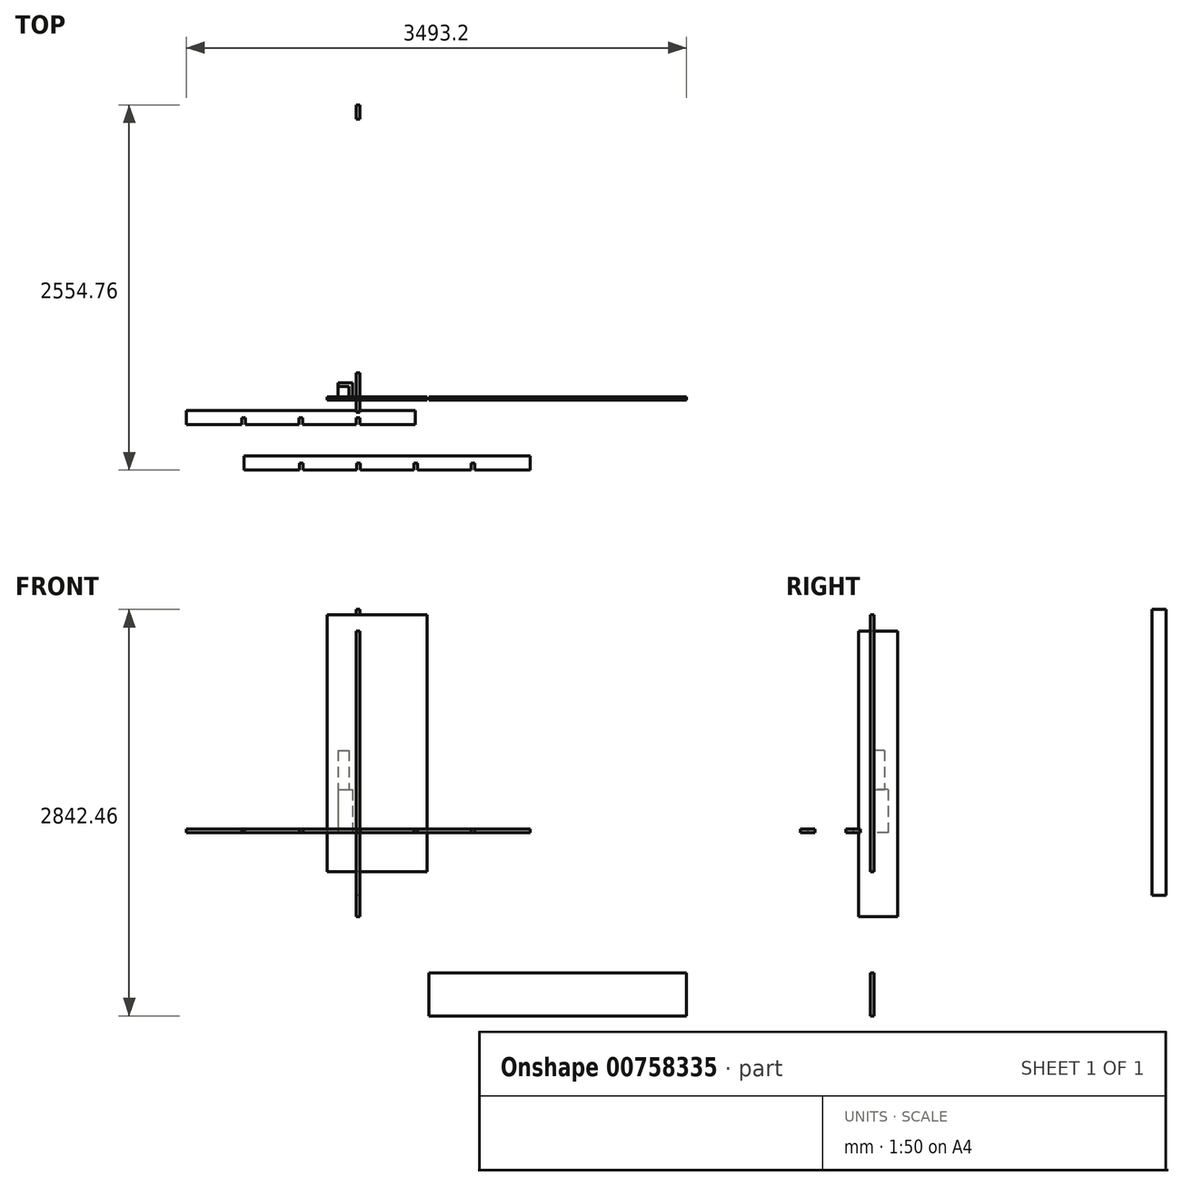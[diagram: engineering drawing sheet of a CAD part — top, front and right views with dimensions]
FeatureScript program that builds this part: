
annotation { "Feature Type Name" : "Feature", "Feature Type Description" : "" }
export const myFeature = defineFeature(function(context is Context, id is Id, definition is map)
    precondition{}
    {
        {
            var Q0;
            Q0=qCreatedBy(makeId("Top.planeOp"),FACE);
            var sketch = newSketch(context, id + "F0", { "sketchPlane" : qUnion([Q0])});
            skLineSegment(sketch, "E0.bottom", {"start": v(-127.05, 96.6) * mm, "end": v(-27.05, 96.6) * mm});
            skLineSegment(sketch, "E0.top", {"start": v(-127.05, -3.4) * mm, "end": v(-27.05, -3.4) * mm});
            skLineSegment(sketch, "E0.left", {"start": v(-127.05, 96.6) * mm, "end": v(-127.05, -3.4) * mm});
            skLineSegment(sketch, "E0.right", {"start": v(-27.05, 96.6) * mm, "end": v(-27.05, -3.4) * mm});
            skSolve(sketch);
        }
        {
            var Q0;
            Q0 = qSketchRegion(id + "F0", true);
            extrude(context, id + "F1", {"entities" : qUnion([Q0]), "depth" : 300 * mm, "offsetDistance" : 25 * mm});
        }
        {
            var Q0;
            Q0=makeQuery(id+"F1.opExtrude","CAP_FACE",FACE,{"disambiguationData":[OSD([sQuery(id+"F0.wireOp",EDGE,"E0.bottom"),sQuery(id+"F0.wireOp",EDGE,"E0.top"),sQuery(id+"F0.wireOp",EDGE,"E0.left"),sQuery(id+"F0.wireOp",EDGE,"E0.right")])],"isStart":false});
            var sketch = newSketch(context, id + "F2", { "sketchPlane" : qUnion([Q0])});
            skLineSegment(sketch, "E1.bottom", {"start": v(-127.05, -3.4) * mm, "end": v(-52.05, -3.4) * mm});
            skLineSegment(sketch, "E1.top", {"start": v(-127.05, 71.6) * mm, "end": v(-52.05, 71.6) * mm});
            skLineSegment(sketch, "E1.left", {"start": v(-127.05, -3.4) * mm, "end": v(-127.05, 71.6) * mm});
            skLineSegment(sketch, "E1.right", {"start": v(-52.05, -3.4) * mm, "end": v(-52.05, 71.6) * mm});
            skSolve(sketch);
        }
        {
            var Q0;
            Q0=makeQuery(id+"F2.imprint","IMPRINT",FACE,{"disambiguationData":[TD([[makeQuery(id+"F2.imprint","IMPRINT",EDGE,{"derivedFrom":sQuery(id+"F2.wireOp",EDGE,"E1.bottom")}),1.0]])]});
            extrude(context, id + "F3", {"entities" : qUnion([Q0]), "operationType" : NewBodyOperationType.ADD, "depth" : 275 * mm, "offsetDistance" : 25 * mm});
        }
        {
            var Q0;
            Q0=qCreatedBy(makeId("Front.planeOp"),FACE);
            var sketch = newSketch(context, id + "F4", { "sketchPlane" : qUnion([Q0])});
            skLineSegment(sketch, "E2.bottom", {"start": v(495.05, 1524.66) * mm, "end": v(-204.95, 1524.66) * mm});
            skLineSegment(sketch, "E2.top", {"start": v(495.05, -275.34) * mm, "end": v(-204.95, -275.34) * mm});
            skLineSegment(sketch, "E2.left", {"start": v(495.05, 1524.66) * mm, "end": v(495.05, -275.34) * mm});
            skLineSegment(sketch, "E2.right", {"start": v(-204.95, 1524.66) * mm, "end": v(-204.95, -275.34) * mm});
            skSolve(sketch);
        }
        {
            var Q0;
            Q0=makeQuery(id+"F4.imprint","IMPRINT",FACE,{"disambiguationData":[TD([[makeQuery(id+"F4.imprint","IMPRINT",EDGE,{"derivedFrom":sQuery(id+"F4.wireOp",EDGE,"E2.bottom")}),1.0]])]});
            extrude(context, id + "F5", {"entities" : qUnion([Q0]), "depth" : 25 * mm, "offsetDistance" : 25 * mm});
        }
        {
            var Q0;
            Q0=qCreatedBy(makeId("Right.planeOp"),FACE);
            var sketch = newSketch(context, id + "F6", { "sketchPlane" : qUnion([Q0])});
            skLineSegment(sketch, "E3.bottom", {"start": v(165.35, 1410.5) * mm, "end": v(-109.65, 1410.5) * mm});
            skLineSegment(sketch, "E3.top", {"start": v(165.35, -589.5) * mm, "end": v(-109.65, -589.5) * mm});
            skLineSegment(sketch, "E3.left", {"start": v(165.35, 1410.5) * mm, "end": v(165.35, -589.5) * mm});
            skLineSegment(sketch, "E3.right", {"start": v(-109.65, 1410.5) * mm, "end": v(-109.65, -589.5) * mm});
            skSolve(sketch);
        }
        {
            var Q0;
            Q0=makeQuery(id+"F6.imprint","IMPRINT",FACE,{"disambiguationData":[TD([[makeQuery(id+"F6.imprint","IMPRINT",EDGE,{"derivedFrom":sQuery(id+"F6.wireOp",EDGE,"E3.bottom")}),1.0]])]});
            extrude(context, id + "F7", {"entities" : qUnion([Q0]), "depth" : 25 * mm, "offsetDistance" : 25 * mm});
        }
        {
            var Q0;
            Q0=qCreatedBy(makeId("Front.planeOp"),FACE);
            var sketch = newSketch(context, id + "F8", { "sketchPlane" : qUnion([Q0])});
            skLineSegment(sketch, "E4.bottom", {"start": v(2305.7, -982.24) * mm, "end": v(505.7, -982.24) * mm});
            skLineSegment(sketch, "E4.top", {"start": v(2305.7, -1282.24) * mm, "end": v(505.7, -1282.24) * mm});
            skLineSegment(sketch, "E4.left", {"start": v(2305.7, -982.24) * mm, "end": v(2305.7, -1282.24) * mm});
            skLineSegment(sketch, "E4.right", {"start": v(505.7, -982.24) * mm, "end": v(505.7, -1282.24) * mm});
            skSolve(sketch);
        }
        {
            var Q0;
            Q0=makeQuery(id+"F8.imprint","IMPRINT",FACE,{"disambiguationData":[TD([[makeQuery(id+"F8.imprint","IMPRINT",EDGE,{"derivedFrom":sQuery(id+"F8.wireOp",EDGE,"E4.bottom")}),1.0]])]});
            extrude(context, id + "F9", {"entities" : qUnion([Q0]), "depth" : 25 * mm, "offsetDistance" : 25 * mm});
        }
        {
            var Q0;
            Q0=qCreatedBy(makeId("Right.planeOp"),FACE);
            var sketch = newSketch(context, id + "F10", { "sketchPlane" : qUnion([Q0])});
            skLineSegment(sketch, "E5.bottom", {"start": v(2041.36, 1560.22) * mm, "end": v(1941.36, 1560.22) * mm});
            skLineSegment(sketch, "E5.top", {"start": v(2041.36, -439.78) * mm, "end": v(1941.36, -439.78) * mm});
            skLineSegment(sketch, "E5.left", {"start": v(2041.36, 1560.22) * mm, "end": v(2041.36, -439.78) * mm});
            skLineSegment(sketch, "E5.right", {"start": v(1941.36, 1560.22) * mm, "end": v(1941.36, -439.78) * mm});
            skSolve(sketch);
        }
        {
            var Q0;
            Q0=makeQuery(id+"F10.imprint","IMPRINT",FACE,{"disambiguationData":[TD([[makeQuery(id+"F10.imprint","IMPRINT",EDGE,{"derivedFrom":sQuery(id+"F10.wireOp",EDGE,"E5.bottom")}),1.0]])]});
            extrude(context, id + "F11", {"entities" : qUnion([Q0]), "depth" : 25 * mm, "offsetDistance" : 25 * mm});
        }
        {
            var Q0;
            Q0=qCreatedBy(makeId("Top.planeOp"),FACE);
            var sketch = newSketch(context, id + "F12", { "sketchPlane" : qUnion([Q0])});
            skLineSegment(sketch, "E6", {"start": v(412.5, -196.5) * mm, "end": v(25, -196.5) * mm});
            skLineSegment(sketch, "E7", {"start": v(25, -196.5) * mm, "end": v(25, -146.5) * mm});
            skLineSegment(sketch, "E8", {"start": v(25, -146.5) * mm, "end": v(0, -146.5) * mm});
            skLineSegment(sketch, "E9", {"start": v(0, -146.5) * mm, "end": v(0, -196.5) * mm});
            skLineSegment(sketch, "E10", {"start": v(0, -196.5) * mm, "end": v(-375, -196.5) * mm});
            skLineSegment(sketch, "E11", {"start": v(-375, -196.5) * mm, "end": v(-375, -146.5) * mm});
            skLineSegment(sketch, "E12", {"start": v(-375, -146.5) * mm, "end": v(-400, -146.5) * mm});
            skLineSegment(sketch, "E13", {"start": v(-400, -146.5) * mm, "end": v(-400, -196.5) * mm});
            skLineSegment(sketch, "E14", {"start": v(-400, -196.5) * mm, "end": v(-775, -196.5) * mm});
            skLineSegment(sketch, "E15", {"start": v(-775, -196.5) * mm, "end": v(-775, -146.5) * mm});
            skLineSegment(sketch, "E16", {"start": v(-775, -146.5) * mm, "end": v(-800, -146.5) * mm});
            skLineSegment(sketch, "E17", {"start": v(-800, -146.5) * mm, "end": v(-800, -196.5) * mm});
            skLineSegment(sketch, "E18", {"start": v(-800, -196.5) * mm, "end": v(-1187.5, -196.5) * mm});
            skLineSegment(sketch, "E19", {"start": v(-1187.5, -196.5) * mm, "end": v(-1187.5, -96.5) * mm});
            skLineSegment(sketch, "E20", {"start": v(-1187.5, -96.5) * mm, "end": v(412.5, -96.5) * mm});
            skLineSegment(sketch, "E21", {"start": v(412.5, -96.5) * mm, "end": v(412.5, -196.5) * mm});
            skSolve(sketch);
        }
        {
            var Q0;
            Q0=makeQuery(id+"F12.imprint","IMPRINT",FACE,{"disambiguationData":[TD([[makeQuery(id+"F12.imprint","IMPRINT",EDGE,{"derivedFrom":sQuery(id+"F12.wireOp",EDGE,"E6")}),-1.0]])]});
            extrude(context, id + "F13", {"entities" : qUnion([Q0]), "depth" : 25 * mm, "offsetDistance" : 25 * mm});
        }
        {
            var Q0;
            Q0=qCreatedBy(makeId("Top.planeOp"),FACE);
            var sketch = newSketch(context, id + "F14", { "sketchPlane" : qUnion([Q0])});
            skLineSegment(sketch, "E22", {"start": v(1215.24, -513.4) * mm, "end": v(827.74, -513.4) * mm});
            skLineSegment(sketch, "E23", {"start": v(827.74, -513.4) * mm, "end": v(827.74, -463.4) * mm});
            skLineSegment(sketch, "E24", {"start": v(827.74, -463.4) * mm, "end": v(802.74, -463.4) * mm});
            skLineSegment(sketch, "E25", {"start": v(802.74, -463.4) * mm, "end": v(802.74, -513.4) * mm});
            skLineSegment(sketch, "E26", {"start": v(802.74, -513.4) * mm, "end": v(427.74, -513.4) * mm});
            skLineSegment(sketch, "E27", {"start": v(427.74, -513.4) * mm, "end": v(427.74, -463.4) * mm});
            skLineSegment(sketch, "E28", {"start": v(427.74, -463.4) * mm, "end": v(402.74, -463.4) * mm});
            skLineSegment(sketch, "E29", {"start": v(402.74, -463.4) * mm, "end": v(402.74, -513.4) * mm});
            skLineSegment(sketch, "E30", {"start": v(402.74, -513.4) * mm, "end": v(27.74, -513.4) * mm});
            skLineSegment(sketch, "E31", {"start": v(27.74, -513.4) * mm, "end": v(27.74, -463.4) * mm});
            skLineSegment(sketch, "E32", {"start": v(27.74, -463.4) * mm, "end": v(2.74, -463.4) * mm});
            skLineSegment(sketch, "E33", {"start": v(2.74, -463.4) * mm, "end": v(2.74, -513.4) * mm});
            skLineSegment(sketch, "E34", {"start": v(2.74, -513.4) * mm, "end": v(-372.26, -513.4) * mm});
            skLineSegment(sketch, "E35", {"start": v(-372.26, -513.4) * mm, "end": v(-372.26, -463.4) * mm});
            skLineSegment(sketch, "E36", {"start": v(-372.26, -463.4) * mm, "end": v(-397.26, -463.4) * mm});
            skLineSegment(sketch, "E37", {"start": v(-397.26, -463.4) * mm, "end": v(-397.26, -513.4) * mm});
            skLineSegment(sketch, "E38", {"start": v(-397.26, -513.4) * mm, "end": v(-784.76, -513.4) * mm});
            skLineSegment(sketch, "E39", {"start": v(-784.76, -513.4) * mm, "end": v(-784.76, -413.4) * mm});
            skLineSegment(sketch, "E40", {"start": v(-784.76, -413.4) * mm, "end": v(1215.24, -413.4) * mm});
            skLineSegment(sketch, "E41", {"start": v(1215.24, -413.4) * mm, "end": v(1215.24, -513.4) * mm});
            skSolve(sketch);
        }
        {
            var Q0;
            Q0=makeQuery(id+"F14.imprint","IMPRINT",FACE,{"disambiguationData":[TD([[makeQuery(id+"F14.imprint","IMPRINT",EDGE,{"derivedFrom":sQuery(id+"F14.wireOp",EDGE,"E22")}),-1.0]])]});
            extrude(context, id + "F15", {"entities" : qUnion([Q0]), "depth" : 25 * mm, "offsetDistance" : 25 * mm});
        }
    });
